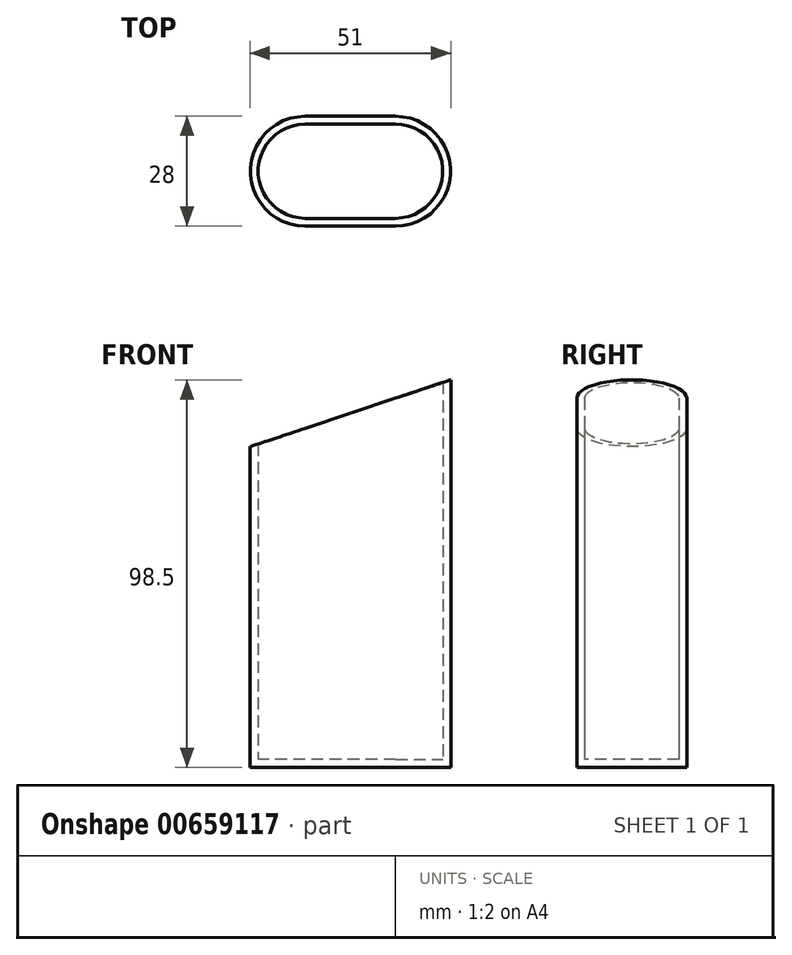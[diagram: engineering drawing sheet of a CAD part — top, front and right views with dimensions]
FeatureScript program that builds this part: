
annotation { "Feature Type Name" : "Feature", "Feature Type Description" : "" }
export const myFeature = defineFeature(function(context is Context, id is Id, definition is map)
    precondition{}
    {
        {
            var Q0;
            Q0=qCreatedBy(makeId("Top.planeOp"),FACE);
            var sketch = newSketch(context, id + "F0", { "sketchPlane" : qUnion([Q0])});
            skLineSegment(sketch, "E0.bottom", {"start": v(11.5, 12) * mm, "end": v(-11.5, 12) * mm});
            skLineSegment(sketch, "E0.top", {"start": v(11.5, -12) * mm, "end": v(-11.5, -12) * mm});
            skLineSegment(sketch, "E0.left", {"start": v(23.5, 0) * mm, "end": v(23.5, 0) * mm});
            skLineSegment(sketch, "E0.right", {"start": v(-23.5, 0) * mm, "end": v(-23.5, 0) * mm});
            skPoint(sketch, "E0.middle", {"position": v(0, 0) * mm});
            skPoint(sketch, "E1.visualSharp", {"position": v(23.5, 12) * mm});
            skArc(sketch, "E1.filletArc", {"start": v(23.5, 0) * mm, "mid": v(19.99, 8.49) * mm, "end": v(11.5, 12) * mm});
            skPoint(sketch, "E2.visualSharp", {"position": v(23.5, -12) * mm});
            skArc(sketch, "E2.filletArc", {"start": v(11.5, -12) * mm, "mid": v(19.99, -8.49) * mm, "end": v(23.5, 0) * mm});
            skPoint(sketch, "E3.visualSharp", {"position": v(-23.5, 12) * mm});
            skArc(sketch, "E3.filletArc", {"start": v(-11.5, 12) * mm, "mid": v(-19.99, 8.49) * mm, "end": v(-23.5, 0) * mm});
            skPoint(sketch, "E4.visualSharp", {"position": v(-23.5, -12) * mm});
            skArc(sketch, "E4.filletArc", {"start": v(-23.5, 0) * mm, "mid": v(-19.99, -8.49) * mm, "end": v(-11.5, -12) * mm});
            skArc(sketch, "E5.0", {"start": v(25.5, 0) * mm, "mid": v(21.4, 9.9) * mm, "end": v(11.5, 14) * mm});
            skArc(sketch, "E5.1", {"start": v(-11.5, 14) * mm, "mid": v(-21.4, -9.9) * mm, "end": v(2.5, 0) * mm});
            skArc(sketch, "E5.2", {"start": v(2.5, 0) * mm, "mid": v(-21.4, 9.9) * mm, "end": v(-11.5, -14) * mm});
            skLineSegment(sketch, "E5.3", {"start": v(11.5, 14) * mm, "end": v(-11.5, 14) * mm});
            skLineSegment(sketch, "E5.4", {"start": v(11.5, -14) * mm, "end": v(-11.5, -14) * mm});
            skArc(sketch, "E5.5", {"start": v(11.5, -14) * mm, "mid": v(21.4, -9.9) * mm, "end": v(25.5, 0) * mm});
            skPoint(sketch, "E6", {"position": v(2.5, 0) * mm});
            skPoint(sketch, "E7", {"position": v(25.5, 0) * mm});
            skSolve(sketch);
        }
        {
            var Q0;
            Q0=makeQuery(id+"F0.imprint","IMPRINT",FACE,{"disambiguationData":[TD([[makeQuery(id+"F0.imprint","IMPRINT",EDGE,{"derivedFrom":sQuery(id+"F0.wireOp",EDGE,"E0.bottom")}),1.0]])]});
            var Q1;
            Q1=makeQuery(id+"F0.imprint","IMPRINT",FACE,{"disambiguationData":[TD([[makeQuery(id+"F0.imprint","IMPRINT",EDGE,{"derivedFrom":sQuery(id+"F0.wireOp",EDGE,"E0.bottom")}),-1.0]])]});
            var Q2;
            {var subQ4=sQuery(id+"F0.wireOp",EDGE,"E3.filletArc");Q2=makeQuery(id+"F0.imprint","IMPRINT",FACE,{"disambiguationData":[TD([[makeQuery(id+"F0.imprint","IMPRINT",EDGE,{"derivedFrom":subQ4}),-1.0]])]});}
            extrude(context, id + "F1", {"entities" : qUnion([Q0, Q1, Q2]), "depth" : 2 * mm});
        }
        {
            var Q0;
            Q0=qSketchRegion(id+"F0",true);
            extrude(context, id + "F2", {"entities" : qUnion([Q0]), "operationType" : NewBodyOperationType.ADD, "depth" : 100 * mm});
        }
        {
            var Q0;
            Q0=makeQuery(id+"F2.opExtrude","SWEPT_FACE",FACE,{"disambiguationData":[OSD([sQuery(id+"F0.wireOp",EDGE,"E5.3")])]});
            var sketch = newSketch(context, id + "F3", { "sketchPlane" : qUnion([Q0])});
            skLineSegment(sketch, "E8", {"start": v(-30, 100) * mm, "end": v(-30, 127.57) * mm});
            skLineSegment(sketch, "E9", {"start": v(-30, 127.57) * mm, "end": v(30, 127.57) * mm});
            skLineSegment(sketch, "E10", {"start": v(30, 127.57) * mm, "end": v(30, 80) * mm});
            skLineSegment(sketch, "E11", {"start": v(30, 80) * mm, "end": v(-30, 100) * mm});
            skSolve(sketch);
        }
        {
            var Q0;
            Q0=qSketchRegion(id+"F3",true);
            extrude(context, id + "F4", {"entities" : qUnion([Q0]), "operationType" : NewBodyOperationType.REMOVE, "endBound" : BoundingType.THROUGH_ALL, "oppositeDirection" : true, "depth" : 25 * mm});
        }
    });
